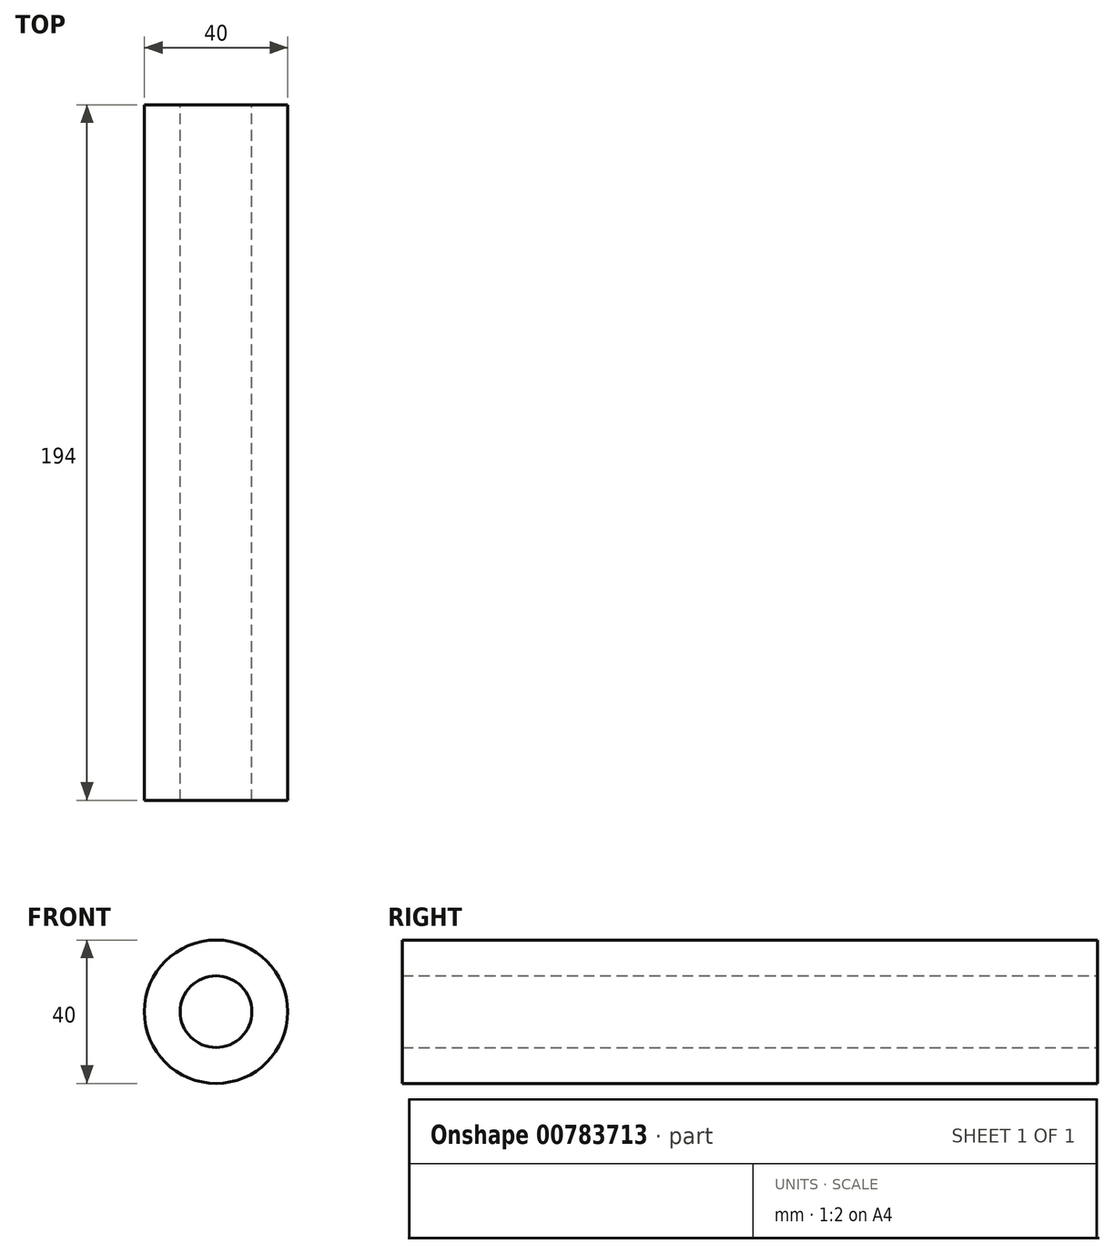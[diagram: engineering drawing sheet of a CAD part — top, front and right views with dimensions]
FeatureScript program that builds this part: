
annotation { "Feature Type Name" : "Feature", "Feature Type Description" : "" }
export const myFeature = defineFeature(function(context is Context, id is Id, definition is map)
    precondition{}
    {
        {
            var Q0;
            Q0=qCreatedBy(makeId("Front.planeOp"),FACE);
            var sketch = newSketch(context, id + "F0", { "sketchPlane" : qUnion([Q0])});
            skCircle(sketch, "E0", {"center": v(0, 0) * mm, "radius": 20 * mm});
            skCircle(sketch, "E1.0", {"center": v(0, 0) * mm, "radius": 10 * mm});
            skSolve(sketch);
        }
        {
            var Q0;
            Q0=makeQuery(id+"F0.imprint","IMPRINT",FACE,{"disambiguationData":[TD([[makeQuery(id+"F0.imprint","IMPRINT",EDGE,{"derivedFrom":sQuery(id+"F0.wireOp",EDGE,"vpl2g39N-VBd4-omPV-kCPW-ZfIFIoekk9ml")}),1.0]])]});
            var Q1;
            Q1=makeQuery(id+"F0.imprint","IMPRINT",FACE,{"disambiguationData":[TD([[makeQuery(id+"F0.imprint","IMPRINT",EDGE,{"derivedFrom":sQuery(id+"F0.wireOp",EDGE,"E0")}),1.0]])]});
            extrude(context, id + "F1", {"entities" : qUnion([Q0, Q1]), "depth" : 194 * mm, "offsetDistance" : 25 * mm});
        }
    });
